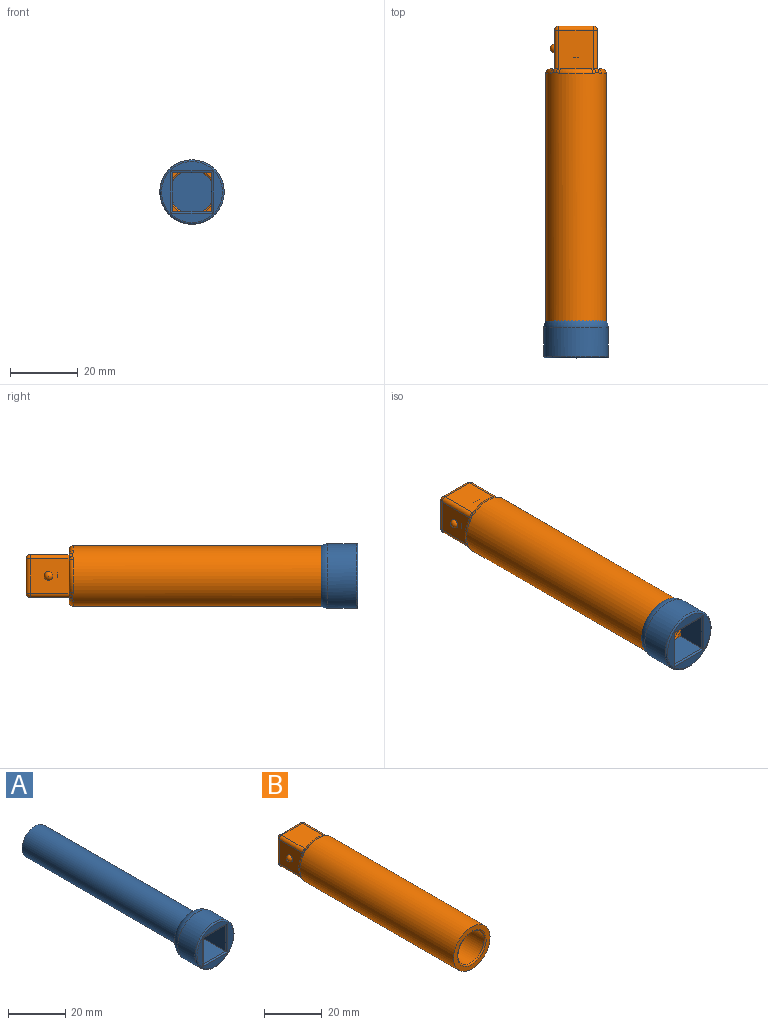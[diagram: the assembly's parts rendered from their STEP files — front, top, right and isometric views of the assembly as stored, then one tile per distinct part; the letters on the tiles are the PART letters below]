
ASSEMBLY  parts=2 mates=1
PART A: 17 faces, bbox 20.6x88.9x20.6 mm
  f0: plane 18.03x18.03mm, normal (0,-1,0), area 100.5mm2, adj f10,f11,f12,f13,f14
  f1: torus R=5.71mm, axis (0,1,0), area 281.8mm2, adj f2,f4,f5,f6,f7,f8,f9
  f2: cylinder r=6.35mm len=76.2mm, axis (0,1,0), area 3040.2mm2, adj f1,f3
  f3: plane 12.7x12.7mm, normal (0,1,0), area 126.7mm2, adj f2
  f4: cylinder r=9.53mm len=19.05mm, axis (0,1,0), area 504.8mm2, adj f1,f14
  f5: plane 11.56x11.44mm, normal (-1,0,0), area 132.1mm2, adj f1,f6,f8,f9,f10
  f6: plane 11.56x11.44mm, normal (0,0,-1), area 132.1mm2, adj f1,f5,f7,f9,f11
  f7: plane 11.56x11.44mm, normal (1,0,0), area 130.8mm2, adj f1,f6,f8,f9,f13,f15
  f8: plane 11.56x11.44mm, normal (0,0,1), area 132.1mm2, adj f1,f5,f7,f9,f12
  f9: plane 11.43x11.43mm, normal (0,-1,0), area 130.5mm2, adj f1,f5,f6,f7,f8
  f10: cylinder r=0.51mm len=12.45mm, axis (0,0,-1), area 9.4mm2, adj f0,f5,f11,f12
  f11: cylinder r=0.51mm len=12.45mm, axis (1,0,0), area 9.4mm2, adj f0,f6,f10,f13
  f12: cylinder r=0.51mm len=12.45mm, axis (-1,0,0), area 9.4mm2, adj f0,f8,f10,f13
  f13: cylinder r=0.51mm len=12.45mm, axis (0,0,1), area 9.4mm2, adj f0,f7,f11,f12
  f14: torus R=9.02mm, axis (0,-1,0), area 46.8mm2, adj f0,f4
  f15: cylinder r=0.64mm len=1.27mm, axis (1,0,0), area 2.5mm2, adj f7,f16
  f16: plane 1.27x1.27mm, normal (1,0,0), area 1.3mm2, adj f15
PART B: 43 faces, bbox 19.3x88.9x19.3 mm
  f0: plane 8.42x1.27mm, normal (0,1,0), area 7mm2, adj f4,f8,f39
  f1: plane 8.42x1.27mm, normal (0,1,0), area 7mm2, adj f4,f9,f31
  f2: plane 8.42x1.27mm, normal (0,1,0), area 7mm2, adj f4,f10,f28
  f3: plane 8.42x1.27mm, normal (0,1,0), area 7mm2, adj f4,f11,f36
  f4: cylinder r=6.48mm len=75.69mm, axis (0,1,0), area 3080.4mm2, adj f0,f1,f2,f3,f7,f13
  f5: cylinder r=8.89mm len=75.12mm, axis (0,1,0), area 4187.1mm2, adj f6,f26,f27,f28,f29,f30,f31,f32
  f6: plane 17.78x17.78mm, normal (0,-1,0), area 95mm2, adj f5,f13
  f7: plane 12.7x12.7mm, normal (0,-1,0), area 130.9mm2, adj f4,f8,f9,f10,f11
  f8: plane 11.47x10.2mm, normal (-1,0,0), area 111.1mm2, adj f0,f7,f16,f22,f25,f37,f41,f42
  f9: plane 11.47x10.2mm, normal (0,0,1), area 116.1mm2, adj f1,f7,f19,f23,f25,f29,f33
  f10: plane 11.47x10.2mm, normal (1,0,0), area 116.1mm2, adj f2,f7,f14,f18,f19,f26,f30
  f11: plane 11.47x10.2mm, normal (0,0,-1), area 116.1mm2, adj f3,f7,f14,f16,f17,f34,f38
  f12: plane 10.16x10.16mm, normal (0,1,0), area 103.2mm2, adj f17,f18,f22,f23
  f13: torus R=6.99mm, axis (0,-1,0), area 33.4mm2, adj f4,f6
  f14: cylinder r=1.27mm len=11.43mm, axis (0,1,0), area 22.8mm2, adj f10,f11,f15,f32
  f15: sphere r=1.27mm, area 2.5mm2, adj f14,f17,f18
  f16: cylinder r=1.27mm len=11.43mm, axis (0,-1,0), area 22.8mm2, adj f8,f11,f20,f40
  f17: cylinder r=1.27mm len=10.16mm, axis (1,0,0), area 20.3mm2, adj f11,f12,f15,f20
  f18: cylinder r=1.27mm len=10.16mm, axis (0,0,1), area 20.3mm2, adj f10,f12,f15,f21
  f19: cylinder r=1.27mm len=11.43mm, axis (0,-1,0), area 22.8mm2, adj f9,f10,f21,f27
  f20: sphere r=1.27mm, area 2.5mm2, adj f16,f17,f22
  f21: sphere r=1.27mm, area 2.5mm2, adj f18,f19,f23
  f22: cylinder r=1.27mm len=10.16mm, axis (0,0,-1), area 20.3mm2, adj f8,f12,f20,f24
  f23: cylinder r=1.27mm len=10.16mm, axis (-1,0,0), area 20.3mm2, adj f9,f12,f21,f24
  f24: sphere r=1.27mm, area 2.5mm2, adj f22,f23,f25
  f25: cylinder r=1.27mm len=11.43mm, axis (0,1,0), area 22.8mm2, adj f8,f9,f24,f35
  f26: bspline ~1.91x1.33mm, area 1.7mm2, adj f5,f10,f27,f28
  f27: bspline ~1.6x1.6mm, area 1.8mm2, adj f5,f19,f26,f29
  f28: torus R=7.62mm, axis (0,-1,0), area 19.7mm2, adj f2,f5,f26,f30
  f29: bspline ~1.91x1.33mm, area 1.7mm2, adj f5,f9,f27,f31
  f30: bspline ~1.91x1.33mm, area 1.7mm2, adj f5,f10,f28,f32
  f31: torus R=7.62mm, axis (0,-1,0), area 19.7mm2, adj f1,f5,f29,f33
  f32: bspline ~1.6x1.6mm, area 1.8mm2, adj f5,f14,f30,f34
  f33: bspline ~1.91x1.33mm, area 1.7mm2, adj f5,f9,f31,f35
  f34: bspline ~1.91x1.33mm, area 1.7mm2, adj f5,f11,f32,f36
  f35: bspline ~1.6x1.6mm, area 1.8mm2, adj f5,f25,f33,f37
  f36: torus R=7.62mm, axis (0,-1,0), area 19.7mm2, adj f3,f5,f34,f38
  f37: bspline ~1.91x1.33mm, area 1.7mm2, adj f5,f8,f35,f39
  f38: bspline ~1.91x1.33mm, area 1.7mm2, adj f5,f11,f36,f40
  f39: torus R=7.62mm, axis (0,-1,0), area 19.7mm2, adj f0,f5,f37,f41
  f40: bspline ~1.6x1.6mm, area 1.8mm2, adj f5,f16,f38,f41
  f41: bspline ~1.91x1.33mm, area 1.7mm2, adj f5,f8,f39,f40
  f42: sphere r=1.27mm, area 10.1mm2, adj f8
PLACE A t=(-28.24,5.67,0.75)mm
PLACE B t=(-28.24,2.16,0.75)mm
MATE slider A.f4 <-> B.f4  axis (0,1,0) through (-28.24,-74.29,0.75)mm
